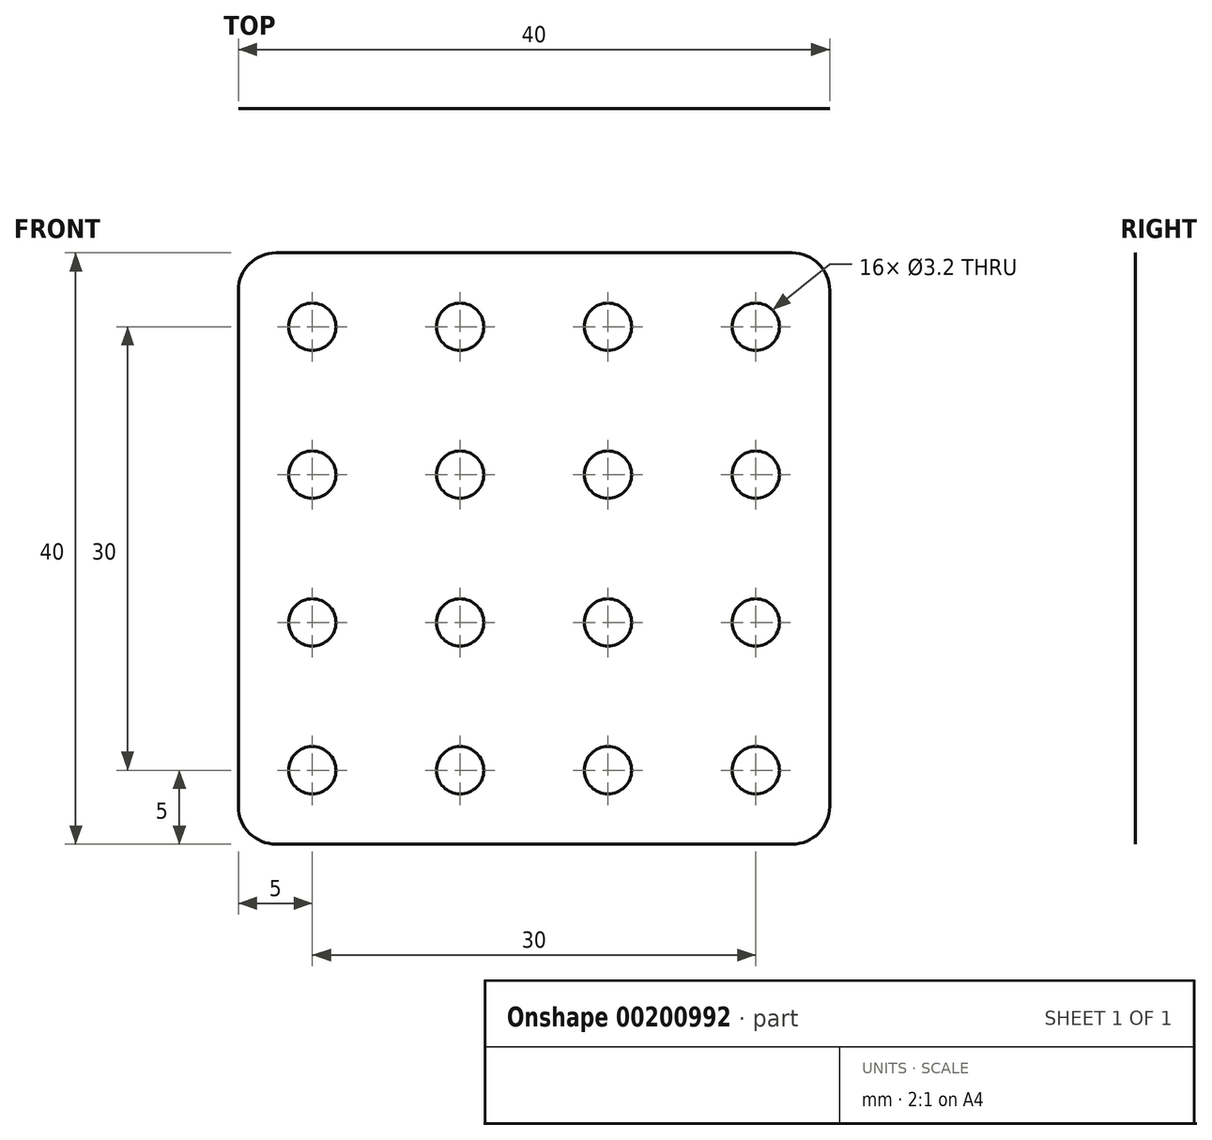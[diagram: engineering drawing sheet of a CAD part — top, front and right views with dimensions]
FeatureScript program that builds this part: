
annotation { "Feature Type Name" : "Feature", "Feature Type Description" : "" }
export const myFeature = defineFeature(function(context is Context, id is Id, definition is map)
    precondition{}
    {
        {
            var Q0;
            Q0=qCreatedBy(makeId("Front.planeOp"),FACE);
            var sketch = newSketch(context, id + "F0", { "sketchPlane" : qUnion([Q0])});
            skLineSegment(sketch, "E0.bottom", {"start": v(2.54, 0) * mm, "end": v(37.46, 0) * mm});
            skLineSegment(sketch, "E0.top", {"start": v(2.54, -40) * mm, "end": v(37.46, -40) * mm});
            skLineSegment(sketch, "E0.left", {"start": v(0, -2.54) * mm, "end": v(0, -37.46) * mm});
            skLineSegment(sketch, "E0.right", {"start": v(40, -2.54) * mm, "end": v(40, -37.46) * mm});
            skCircle(sketch, "E1", {"center": v(5, -5) * mm, "radius": 1.6 * mm});
            skPoint(sketch, "E2.visualSharp", {"position": v(0, 0) * mm});
            skArc(sketch, "E2.filletArc", {"start": v(2.54, 0) * mm, "mid": v(0.74, -0.74) * mm, "end": v(0, -2.54) * mm});
            skPoint(sketch, "E3.visualSharp", {"position": v(40, 0) * mm});
            skArc(sketch, "E3.filletArc", {"start": v(40, -2.54) * mm, "mid": v(39.26, -0.74) * mm, "end": v(37.46, 0) * mm});
            skPoint(sketch, "E4.visualSharp", {"position": v(40, -40) * mm});
            skArc(sketch, "E4.filletArc", {"start": v(37.46, -40) * mm, "mid": v(39.26, -39.26) * mm, "end": v(40, -37.46) * mm});
            skPoint(sketch, "E5.visualSharp", {"position": v(0, -40) * mm});
            skArc(sketch, "E5.filletArc", {"start": v(0, -37.46) * mm, "mid": v(0.74, -39.26) * mm, "end": v(2.54, -40) * mm});
            skCircle(sketch, "E6.0.1.0", {"center": v(5, -15) * mm, "radius": 1.6 * mm});
            skCircle(sketch, "E6.0.2.0", {"center": v(5, -25) * mm, "radius": 1.6 * mm});
            skCircle(sketch, "E6.0.3.0", {"center": v(5, -35) * mm, "radius": 1.6 * mm});
            skCircle(sketch, "E6.1.0.0", {"center": v(15, -5) * mm, "radius": 1.6 * mm});
            skCircle(sketch, "E6.1.1.0", {"center": v(15, -15) * mm, "radius": 1.6 * mm});
            skCircle(sketch, "E6.1.2.0", {"center": v(15, -25) * mm, "radius": 1.6 * mm});
            skCircle(sketch, "E6.1.3.0", {"center": v(15, -35) * mm, "radius": 1.6 * mm});
            skCircle(sketch, "E6.2.0.0", {"center": v(25, -5) * mm, "radius": 1.6 * mm});
            skCircle(sketch, "E6.2.1.0", {"center": v(25, -15) * mm, "radius": 1.6 * mm});
            skCircle(sketch, "E6.2.2.0", {"center": v(25, -25) * mm, "radius": 1.6 * mm});
            skCircle(sketch, "E6.2.3.0", {"center": v(25, -35) * mm, "radius": 1.6 * mm});
            skCircle(sketch, "E6.3.0.0", {"center": v(35, -5) * mm, "radius": 1.6 * mm});
            skCircle(sketch, "E6.3.1.0", {"center": v(35, -15) * mm, "radius": 1.6 * mm});
            skCircle(sketch, "E6.3.2.0", {"center": v(35, -25) * mm, "radius": 1.6 * mm});
            skCircle(sketch, "E6.3.3.0", {"center": v(35, -35) * mm, "radius": 1.6 * mm});
            skLineSegment(sketch, "E6.direction1", {"start": v(5, -5) * mm, "end": v(15, -5) * mm, "construction": true});
            skLineSegment(sketch, "E6.direction2", {"start": v(5, -5) * mm, "end": v(5, -15) * mm, "construction": true});
            skSolve(sketch);
        }
        {
            var Q0;
            Q0=makeQuery(id+"F0.imprint","IMPRINT",FACE,{"disambiguationData":[TD([[makeQuery(id+"F0.imprint","IMPRINT",EDGE,{"derivedFrom":sQuery(id+"F0.wireOp",EDGE,"E0.bottom")}),-1.0]])]});
            extrude(context, id + "F1", {"entities" : qUnion([Q0]), "depth" : 1 / 203.2 * mm});
        }
    });
